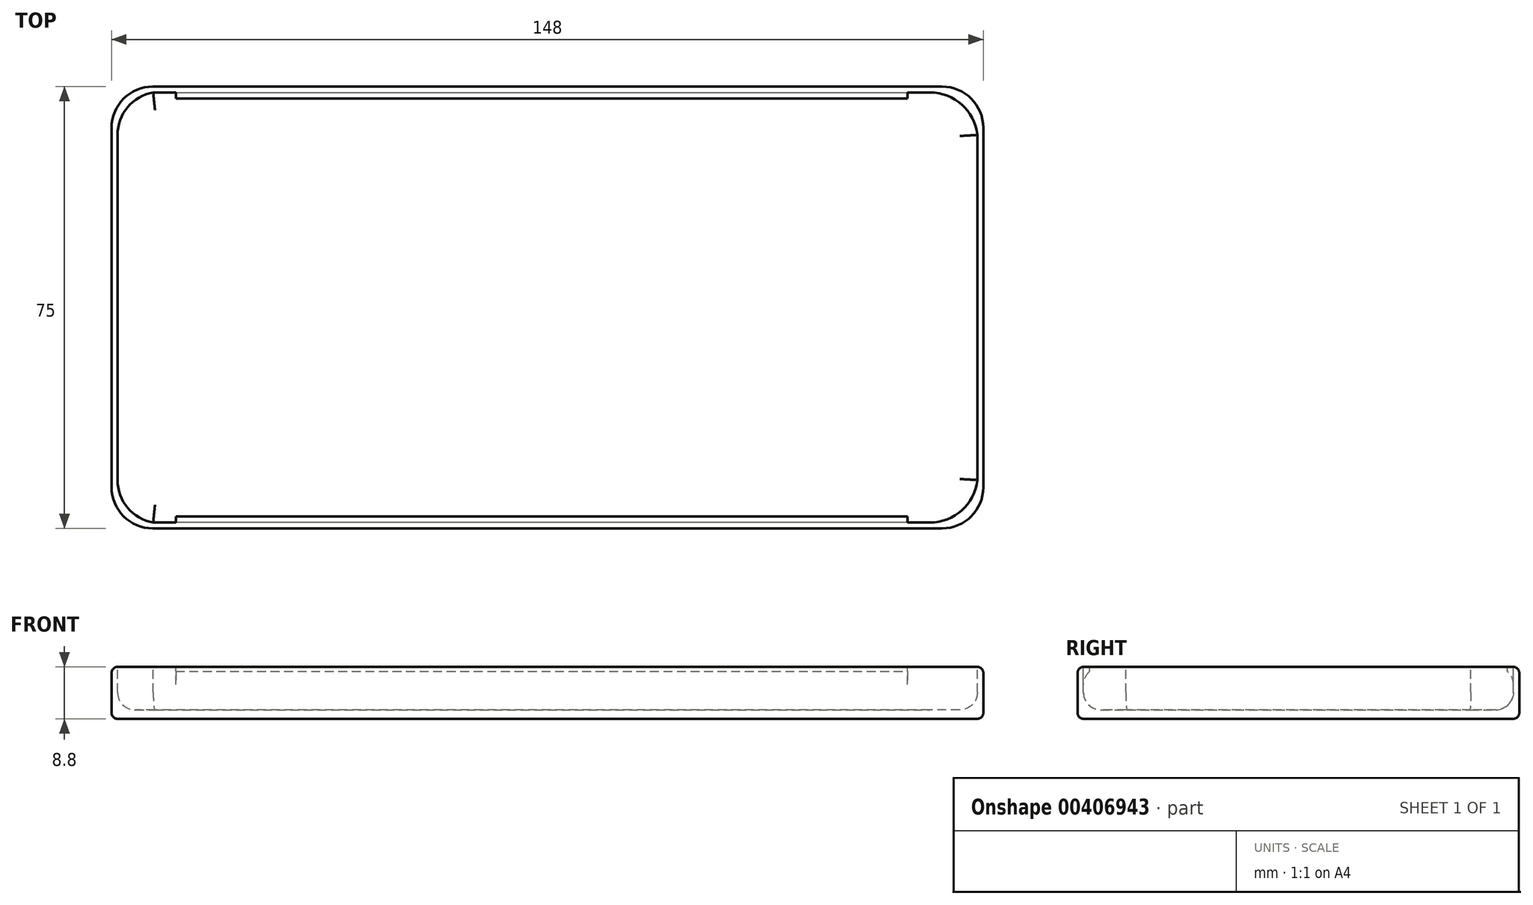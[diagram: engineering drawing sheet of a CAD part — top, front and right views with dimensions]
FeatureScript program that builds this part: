
annotation { "Feature Type Name" : "Feature", "Feature Type Description" : "" }
export const myFeature = defineFeature(function(context is Context, id is Id, definition is map)
    precondition{}
    {
        {
            var Q0;
            Q0=qCreatedBy(makeId("Top.planeOp"),FACE);
            var sketch = newSketch(context, id + "F0", { "sketchPlane" : qUnion([Q0])});
            skLineSegment(sketch, "E0.bottom", {"start": v(-80.86, -49.7) * mm, "end": v(67.14, -49.7) * mm});
            skLineSegment(sketch, "E0.top", {"start": v(-80.86, 25.3) * mm, "end": v(67.14, 25.3) * mm});
            skLineSegment(sketch, "E0.left", {"start": v(-80.86, -49.7) * mm, "end": v(-80.86, 25.3) * mm});
            skLineSegment(sketch, "E0.right", {"start": v(67.14, -49.7) * mm, "end": v(67.14, 25.3) * mm});
            skSolve(sketch);
        }
        {
            var Q0;
            Q0=makeQuery(id+"F0.imprint","IMPRINT",FACE,{"disambiguationData":[TD([[makeQuery(id+"F0.imprint","IMPRINT",EDGE,{"derivedFrom":sQuery(id+"F0.wireOp",EDGE,"E0.bottom")}),1.0]])]});
            extrude(context, id + "F1", {"entities" : qUnion([Q0]), "depth" : 8.8 * mm});
        }
        {
            var Q0;
            Q0=makeQuery(id+"F1.opExtrude","SWEPT_EDGE",EDGE,{"disambiguationData":[OSD([sQuery(id+"F0.wireOp",EDGE,"E0.bottom"),sQuery(id+"F0.wireOp",EDGE,"E0.right")])]});
            var Q1;
            Q1=makeQuery(id+"F1.opExtrude","SWEPT_EDGE",EDGE,{"disambiguationData":[OSD([sQuery(id+"F0.wireOp",EDGE,"E0.top"),sQuery(id+"F0.wireOp",EDGE,"E0.right")])]});
            var Q2;
            Q2=makeQuery(id+"F1.opExtrude","SWEPT_EDGE",EDGE,{"disambiguationData":[OSD([sQuery(id+"F0.wireOp",EDGE,"E0.bottom"),sQuery(id+"F0.wireOp",EDGE,"E0.left")])]});
            var Q3;
            Q3=makeQuery(id+"F1.opExtrude","SWEPT_EDGE",EDGE,{"disambiguationData":[OSD([sQuery(id+"F0.wireOp",EDGE,"E0.top"),sQuery(id+"F0.wireOp",EDGE,"E0.left")])]});
            fillet(context, id + "F2", {"entities" : qUnion([Q0, Q1, Q2, Q3]), "radius" : 7 * mm, "tangentPropagation" : true, "allowEdgeOverflow" : false});
        }
        {
            var Q0;
            Q0=makeQuery(id+"F1.opExtrude","CAP_FACE",FACE,{"disambiguationData":[OSD([sQuery(id+"F0.wireOp",EDGE,"E0.bottom"),sQuery(id+"F0.wireOp",EDGE,"E0.top"),sQuery(id+"F0.wireOp",EDGE,"E0.left"),sQuery(id+"F0.wireOp",EDGE,"E0.right")])],"isStart":true});
            fillet(context, id + "F3", {"entities" : qUnion([Q0]), "radius" : 1 * mm, "tangentPropagation" : true, "allowEdgeOverflow" : false});
        }
        {
            var Q0;
            Q0=makeQuery(id+"F1.opExtrude","CAP_EDGE",EDGE,{"disambiguationData":[OSD([sQuery(id+"F0.wireOp",EDGE,"E0.bottom")])],"isStart":false});
            var Q1;
            {var subQ0=sQuery(id+"F0.wireOp",EDGE,"E0.left");var subQ1=sQuery(id+"F0.wireOp",EDGE,"E0.bottom");Q1=makeQuery(id+"F2.opFillet","BLEND_EDGE",EDGE,{"blendedFrom":[makeQuery(id+"F1.opExtrude","SWEPT_EDGE",EDGE,{"disambiguationData":[OSD([subQ1,subQ0])]}),makeQuery(id+"F1.opExtrude","CAP_FACE",FACE,{"disambiguationData":[OSD([subQ1,sQuery(id+"F0.wireOp",EDGE,"E0.top"),subQ0,sQuery(id+"F0.wireOp",EDGE,"E0.right")])],"isStart":false})],"blendedInto":[makeQuery(id+"F1.opExtrude","CAP_FACE",FACE,{"disambiguationData":[OSD([subQ1,sQuery(id+"F0.wireOp",EDGE,"E0.top"),subQ0,sQuery(id+"F0.wireOp",EDGE,"E0.right")])],"isStart":false})]});}
            var Q2;
            Q2=makeQuery(id+"F1.opExtrude","CAP_EDGE",EDGE,{"disambiguationData":[OSD([sQuery(id+"F0.wireOp",EDGE,"E0.left")])],"isStart":false});
            var Q3;
            {var subQ0=sQuery(id+"F0.wireOp",EDGE,"E0.left");var subQ1=sQuery(id+"F0.wireOp",EDGE,"E0.top");Q3=makeQuery(id+"F2.opFillet","BLEND_EDGE",EDGE,{"blendedFrom":[makeQuery(id+"F1.opExtrude","SWEPT_EDGE",EDGE,{"disambiguationData":[OSD([subQ1,subQ0])]}),makeQuery(id+"F1.opExtrude","CAP_FACE",FACE,{"disambiguationData":[OSD([sQuery(id+"F0.wireOp",EDGE,"E0.bottom"),subQ1,subQ0,sQuery(id+"F0.wireOp",EDGE,"E0.right")])],"isStart":false})],"blendedInto":[makeQuery(id+"F1.opExtrude","CAP_FACE",FACE,{"disambiguationData":[OSD([sQuery(id+"F0.wireOp",EDGE,"E0.bottom"),subQ1,subQ0,sQuery(id+"F0.wireOp",EDGE,"E0.right")])],"isStart":false})]});}
            var Q4;
            Q4=makeQuery(id+"F1.opExtrude","CAP_EDGE",EDGE,{"disambiguationData":[OSD([sQuery(id+"F0.wireOp",EDGE,"E0.top")])],"isStart":false});
            var Q5;
            Q5=makeQuery(id+"F1.opExtrude","CAP_EDGE",EDGE,{"disambiguationData":[OSD([sQuery(id+"F0.wireOp",EDGE,"E0.right")])],"isStart":false});
            var Q6;
            {var subQ0=sQuery(id+"F0.wireOp",EDGE,"E0.right");var subQ1=sQuery(id+"F0.wireOp",EDGE,"E0.top");Q6=makeQuery(id+"F2.opFillet","BLEND_EDGE",EDGE,{"blendedFrom":[makeQuery(id+"F1.opExtrude","SWEPT_EDGE",EDGE,{"disambiguationData":[OSD([subQ1,subQ0])]}),makeQuery(id+"F1.opExtrude","CAP_FACE",FACE,{"disambiguationData":[OSD([sQuery(id+"F0.wireOp",EDGE,"E0.bottom"),subQ1,sQuery(id+"F0.wireOp",EDGE,"E0.left"),subQ0])],"isStart":false})],"blendedInto":[makeQuery(id+"F1.opExtrude","CAP_FACE",FACE,{"disambiguationData":[OSD([sQuery(id+"F0.wireOp",EDGE,"E0.bottom"),subQ1,sQuery(id+"F0.wireOp",EDGE,"E0.left"),subQ0])],"isStart":false})]});}
            var Q7;
            {var subQ0=sQuery(id+"F0.wireOp",EDGE,"E0.right");var subQ1=sQuery(id+"F0.wireOp",EDGE,"E0.bottom");Q7=makeQuery(id+"F2.opFillet","BLEND_EDGE",EDGE,{"blendedFrom":[makeQuery(id+"F1.opExtrude","SWEPT_EDGE",EDGE,{"disambiguationData":[OSD([subQ1,subQ0])]}),makeQuery(id+"F1.opExtrude","CAP_FACE",FACE,{"disambiguationData":[OSD([subQ1,sQuery(id+"F0.wireOp",EDGE,"E0.top"),sQuery(id+"F0.wireOp",EDGE,"E0.left"),subQ0])],"isStart":false})],"blendedInto":[makeQuery(id+"F1.opExtrude","CAP_FACE",FACE,{"disambiguationData":[OSD([subQ1,sQuery(id+"F0.wireOp",EDGE,"E0.top"),sQuery(id+"F0.wireOp",EDGE,"E0.left"),subQ0])],"isStart":false})]});}
            fillet(context, id + "F4", {"entities" : qUnion([Q0, Q1, Q2, Q3, Q4, Q5, Q6, Q7]), "radius" : 1 * mm, "tangentPropagation" : true, "allowEdgeOverflow" : false});
        }
        {
            var Q0;
            Q0=makeQuery(id+"F1.opExtrude","CAP_FACE",FACE,{"disambiguationData":[OSD([sQuery(id+"F0.wireOp",EDGE,"E0.bottom"),sQuery(id+"F0.wireOp",EDGE,"E0.top"),sQuery(id+"F0.wireOp",EDGE,"E0.left"),sQuery(id+"F0.wireOp",EDGE,"E0.right")])],"isStart":false});
            var sketch = newSketch(context, id + "F5", { "sketchPlane" : qUnion([Q0])});
            skLineSegment(sketch, "E1", {"start": v(-73.78, 24.3) * mm, "end": v(-69.95, 24.3) * mm});
            skLineSegment(sketch, "E2", {"start": v(-69.95, 24.3) * mm, "end": v(-69.95, 23.27) * mm});
            skLineSegment(sketch, "E3", {"start": v(-69.95, 23.27) * mm, "end": v(54.25, 23.27) * mm});
            skLineSegment(sketch, "E4", {"start": v(54.25, 23.27) * mm, "end": v(54.25, 24.3) * mm});
            skLineSegment(sketch, "E5", {"start": v(54.25, 24.3) * mm, "end": v(58.08, 24.3) * mm});
            skLineSegment(sketch, "E6", {"start": v(-79.86, 17.07) * mm, "end": v(-79.86, -41.49) * mm});
            skLineSegment(sketch, "E7", {"start": v(66.14, 17.07) * mm, "end": v(66.14, -41.49) * mm});
            skLineSegment(sketch, "E8", {"start": v(-73.78, -48.7) * mm, "end": v(-69.95, -48.7) * mm});
            skLineSegment(sketch, "E9", {"start": v(-69.95, -48.7) * mm, "end": v(-69.95, -47.68) * mm});
            skLineSegment(sketch, "E10", {"start": v(-69.95, -47.68) * mm, "end": v(54.25, -47.68) * mm});
            skLineSegment(sketch, "E11", {"start": v(54.25, -47.68) * mm, "end": v(54.25, -48.7) * mm});
            skLineSegment(sketch, "E12", {"start": v(54.25, -48.7) * mm, "end": v(58.08, -48.7) * mm});
            skLineSegment(sketch, "E13", {"start": v(66.14, -12.2) * mm, "end": v(-79.86, -12.2) * mm, "construction": true});
            skArc(sketch, "E14", {"start": v(58.08, 24.3) * mm, "mid": v(63.49, 22.22) * mm, "end": v(66.14, 17.07) * mm});
            skLineSegment(sketch, "E15", {"start": v(-7.85, 23.27) * mm, "end": v(-7.85, -47.68) * mm, "construction": true});
            skArc(sketch, "E16", {"start": v(58.08, -48.7) * mm, "mid": v(63.49, -46.64) * mm, "end": v(66.14, -41.49) * mm});
            skArc(sketch, "E17", {"start": v(-79.86, -41.49) * mm, "mid": v(-78.14, -46.2) * mm, "end": v(-73.78, -48.7) * mm});
            skArc(sketch, "E18", {"start": v(-79.86, 17.07) * mm, "mid": v(-78.14, 21.8) * mm, "end": v(-73.78, 24.3) * mm});
            skSolve(sketch);
        }
        {
            var Q0;
            Q0 = qSketchRegion(id + "F5", true);
            extrude(context, id + "F6", {"entities" : qUnion([Q0]), "operationType" : NewBodyOperationType.REMOVE, "oppositeDirection" : true, "depth" : 3 * mm});
        }
        {
            var Q0;
            Q0=makeQuery(id+"F6.boolean.opBoolean","COPY",FACE,{"derivedFrom":makeQuery(id+"F6.opExtrude","CAP_FACE",FACE,{"disambiguationData":[OSD([sQuery(id+"F5.wireOp",EDGE,"E1"),sQuery(id+"F5.wireOp",EDGE,"E2"),sQuery(id+"F5.wireOp",EDGE,"E3"),sQuery(id+"F5.wireOp",EDGE,"E4"),sQuery(id+"F5.wireOp",EDGE,"E5"),sQuery(id+"F5.wireOp",EDGE,"E6"),sQuery(id+"F5.wireOp",EDGE,"E7"),sQuery(id+"F5.wireOp",EDGE,"E8"),sQuery(id+"F5.wireOp",EDGE,"E9"),sQuery(id+"F5.wireOp",EDGE,"E10"),sQuery(id+"F5.wireOp",EDGE,"E11"),sQuery(id+"F5.wireOp",EDGE,"E12"),sQuery(id+"F5.wireOp",EDGE,"E14"),sQuery(id+"F5.wireOp",EDGE,"E16"),sQuery(id+"F5.wireOp",EDGE,"E17"),sQuery(id+"F5.wireOp",EDGE,"E18")])],"isStart":false})});
            var sketch = newSketch(context, id + "F7", { "sketchPlane" : qUnion([Q0])});
            skLineSegment(sketch, "E19", {"start": v(58.08, -48.7) * mm, "end": v(-73.78, -48.7) * mm});
            skLineSegment(sketch, "E20", {"start": v(-79.86, -41.49) * mm, "end": v(-79.86, 17.07) * mm});
            skLineSegment(sketch, "E21", {"start": v(-73.78, 24.3) * mm, "end": v(58.08, 24.3) * mm});
            skLineSegment(sketch, "E22", {"start": v(66.14, 17.07) * mm, "end": v(66.14, -41.49) * mm});
            skArc(sketch, "E23", {"start": v(58.08, 24.3) * mm, "mid": v(63.49, 22.22) * mm, "end": v(66.14, 17.07) * mm});
            skArc(sketch, "E24", {"start": v(58.08, -48.7) * mm, "mid": v(63.49, -46.64) * mm, "end": v(66.14, -41.49) * mm});
            skArc(sketch, "E25", {"start": v(-79.86, 17.07) * mm, "mid": v(-78.14, 21.8) * mm, "end": v(-73.78, 24.3) * mm});
            skArc(sketch, "E26", {"start": v(-79.86, -41.49) * mm, "mid": v(-78.14, -46.2) * mm, "end": v(-73.78, -48.7) * mm});
            skSolve(sketch);
        }
        {
            var Q0;
            Q0 = qSketchRegion(id + "F7", true);
            extrude(context, id + "F8", {"entities" : qUnion([Q0]), "operationType" : NewBodyOperationType.REMOVE, "oppositeDirection" : true, "depth" : 4.3 * mm});
        }
        {
            var Q0;
            Q0=makeQuery(id+"F6.boolean.opBoolean","COPY",FACE,{"derivedFrom":makeQuery(id+"F6.opExtrude","SWEPT_FACE",FACE,{"disambiguationData":[OSD([sQuery(id+"F5.wireOp",EDGE,"E11")])]})});
            var sketch = newSketch(context, id + "F9", { "sketchPlane" : qUnion([Q0])});
            skArc(sketch, "E27", {"start": v(-47.68, 8.04) * mm, "mid": v(-48.44, 7.03) * mm, "end": v(-48.7, 5.8) * mm});
            skLineSegment(sketch, "E28", {"start": v(-47.68, 8.04) * mm, "end": v(-47.68, 5.8) * mm});
            skLineSegment(sketch, "E29", {"start": v(-47.68, 5.8) * mm, "end": v(-48.7, 5.8) * mm});
            skSolve(sketch);
        }
        {
            var Q0;
            Q0 = qSketchRegion(id + "F9", true);
            extrude(context, id + "F10", {"entities" : qUnion([Q0]), "operationType" : NewBodyOperationType.REMOVE, "oppositeDirection" : true, "depth" : 124.2 * mm});
        }
        {
            var Q0;
            Q0=makeQuery(id+"F6.boolean.opBoolean","COPY",FACE,{"derivedFrom":makeQuery(id+"F6.opExtrude","SWEPT_FACE",FACE,{"disambiguationData":[OSD([sQuery(id+"F5.wireOp",EDGE,"E2")])]})});
            var sketch = newSketch(context, id + "F11", { "sketchPlane" : qUnion([Q0])});
            skArc(sketch, "E30", {"start": v(-23.27, 8.04) * mm, "mid": v(-24.02, 7.03) * mm, "end": v(-24.3, 5.8) * mm});
            skLineSegment(sketch, "E31", {"start": v(-24.3, 5.8) * mm, "end": v(-23.27, 5.8) * mm});
            skLineSegment(sketch, "E32", {"start": v(-23.27, 5.8) * mm, "end": v(-23.27, 8.04) * mm});
            skSolve(sketch);
        }
        {
            var Q0;
            Q0 = qSketchRegion(id + "F11", true);
            extrude(context, id + "F12", {"entities" : qUnion([Q0]), "operationType" : NewBodyOperationType.REMOVE, "oppositeDirection" : true, "depth" : 124.2 * mm});
        }
        {
            var Q0;
            Q0=makeQuery(id+"F8.boolean.opBoolean","COPY",FACE,{"derivedFrom":makeQuery(id+"F8.opExtrude","CAP_FACE",FACE,{"disambiguationData":[OSD([sQuery(id+"F7.wireOp",EDGE,"E19"),sQuery(id+"F7.wireOp",EDGE,"E20"),sQuery(id+"F7.wireOp",EDGE,"E21"),sQuery(id+"F7.wireOp",EDGE,"E22"),sQuery(id+"F7.wireOp",EDGE,"E23"),sQuery(id+"F7.wireOp",EDGE,"E24"),sQuery(id+"F7.wireOp",EDGE,"E25"),sQuery(id+"F7.wireOp",EDGE,"E26")])],"isStart":false})});
            fillet(context, id + "F13", {"entities" : qUnion([Q0]), "radius" : 3 * mm, "tangentPropagation" : true, "allowEdgeOverflow" : false});
        }
    });
